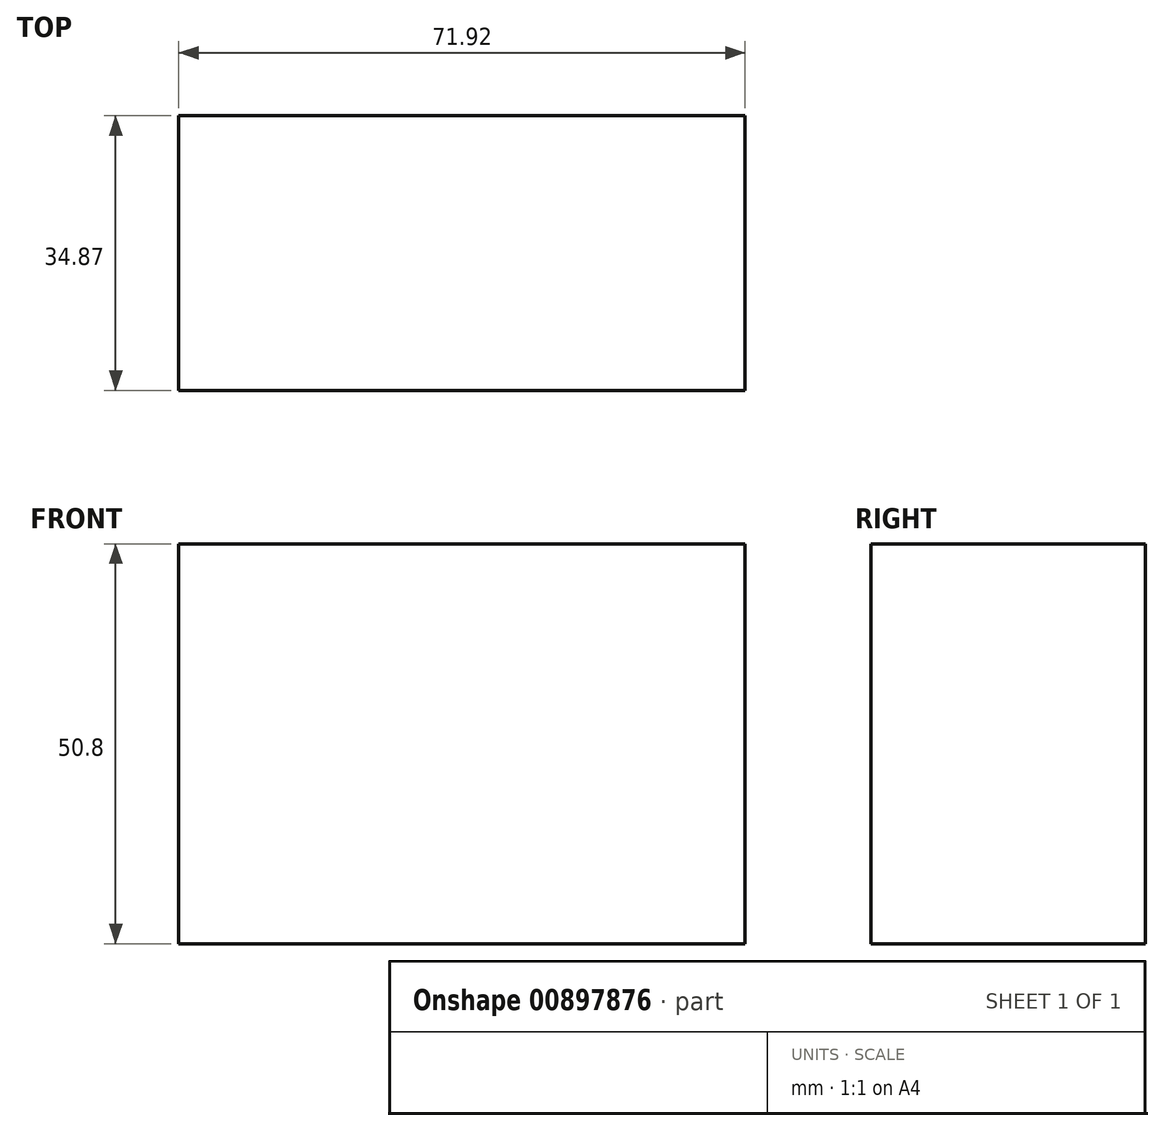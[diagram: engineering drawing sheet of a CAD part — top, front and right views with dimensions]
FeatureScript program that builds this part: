
annotation { "Feature Type Name" : "Feature", "Feature Type Description" : "" }
export const myFeature = defineFeature(function(context is Context, id is Id, definition is map)
    precondition{}
    {
        {
            var Q0;
            Q0=qCreatedBy(makeId("Top.planeOp"),FACE);
            var sketch = newSketch(context, id + "F0", { "sketchPlane" : qUnion([Q0])});
            skLineSegment(sketch, "E0.bottom", {"start": v(-60.09, 16.66) * mm, "end": v(11.83, 16.66) * mm});
            skLineSegment(sketch, "E0.top", {"start": v(-60.09, -18.21) * mm, "end": v(11.83, -18.21) * mm});
            skLineSegment(sketch, "E0.left", {"start": v(-60.09, 16.66) * mm, "end": v(-60.09, -18.21) * mm});
            skLineSegment(sketch, "E0.right", {"start": v(11.83, 16.66) * mm, "end": v(11.83, -18.21) * mm});
            skSolve(sketch);
        }
        {
            var Q0;
            Q0=makeQuery(id+"F0.imprint","IMPRINT",FACE,{"disambiguationData":[TD([[makeQuery(id+"F0.imprint","IMPRINT",EDGE,{"derivedFrom":sQuery(id+"F0.wireOp",EDGE,"E0.bottom")}),-1.0]])]});
            extrude(context, id + "F1", {"entities" : qUnion([Q0]), "depth" : 50.8 * mm, "offsetDistance" : 25.4 * mm});
        }
    });
